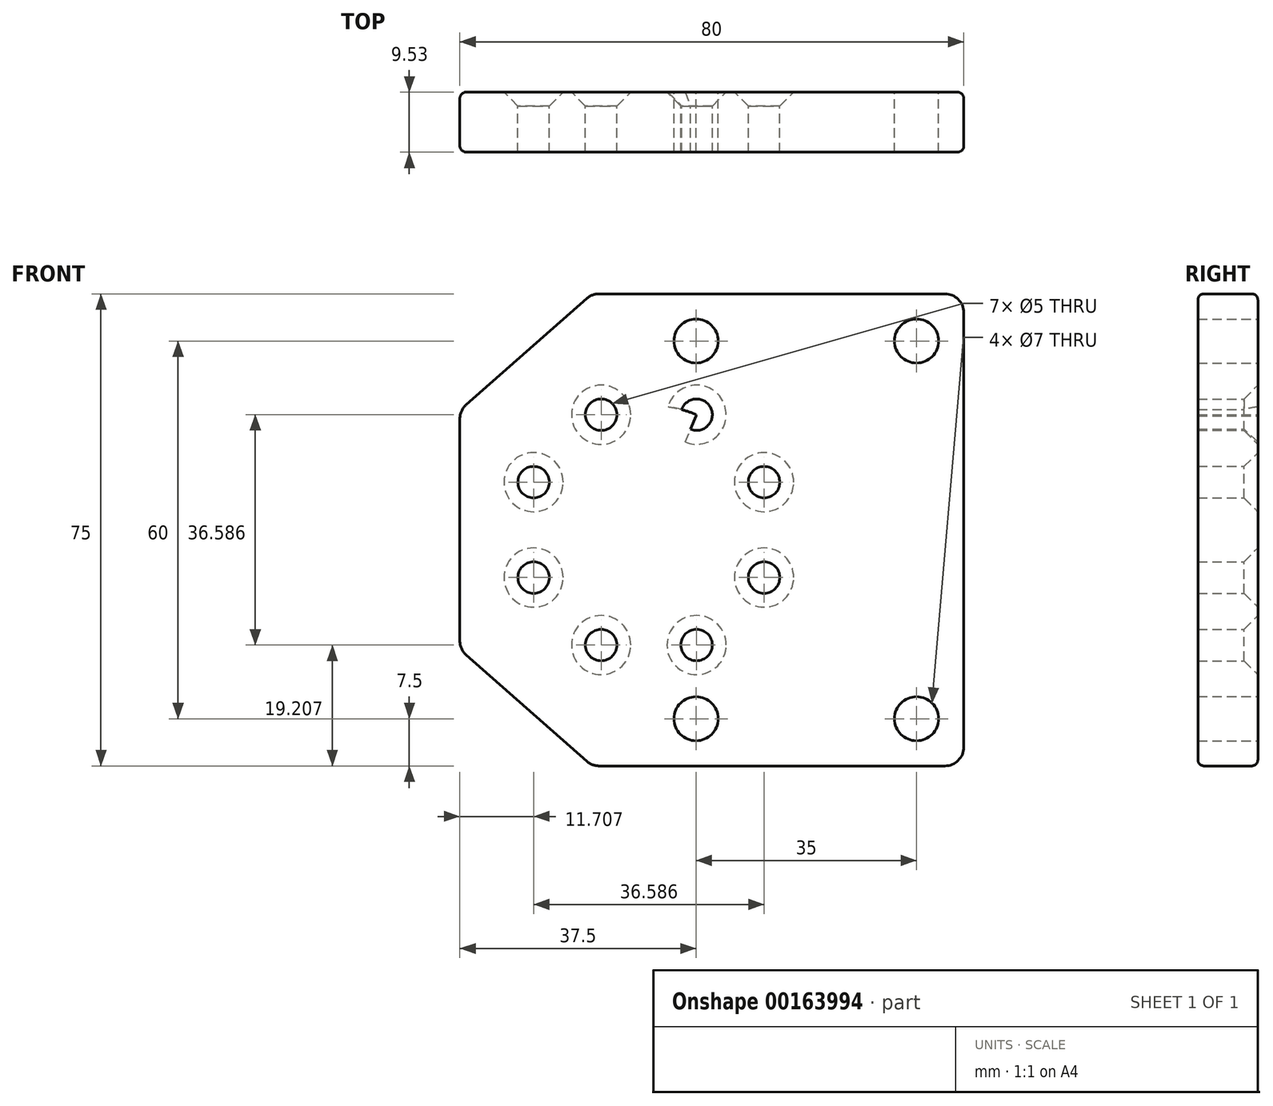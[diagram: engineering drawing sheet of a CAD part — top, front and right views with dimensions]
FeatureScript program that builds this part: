
annotation { "Feature Type Name" : "Feature", "Feature Type Description" : "" }
export const myFeature = defineFeature(function(context is Context, id is Id, definition is map)
    precondition{}
    {
        {
            var Q0;
            Q0=qCreatedBy(makeId("Front.planeOp"),FACE);
            var sketch = newSketch(context, id + "F0", { "sketchPlane" : qUnion([Q0])});
            skPoint(sketch, "E0.middle", {"position": v(0, 0) * mm});
            skCircle(sketch, "E1", {"center": v(0, 0) * mm, "radius": 19.8 * mm});
            skCircle(sketch, "E2", {"center": v(-7.58, 18.3) * mm, "radius": 2.5 * mm});
            skCircle(sketch, "E3", {"center": v(7.58, 18.3) * mm, "radius": 2.5 * mm});
            skCircle(sketch, "E4", {"center": v(18.3, 7.58) * mm, "radius": 2.5 * mm});
            skCircle(sketch, "E5", {"center": v(18.3, -7.58) * mm, "radius": 2.5 * mm});
            skCircle(sketch, "E6", {"center": v(7.58, -18.3) * mm, "radius": 2.5 * mm});
            skCircle(sketch, "E7", {"center": v(-7.58, -18.3) * mm, "radius": 2.5 * mm});
            skCircle(sketch, "E8", {"center": v(-18.3, -7.58) * mm, "radius": 2.5 * mm});
            skCircle(sketch, "E9", {"center": v(-18.3, 7.58) * mm, "radius": 2.5 * mm});
            skLineSegment(sketch, "E10", {"start": v(0, 0) * mm, "end": v(33.82, 81.64) * mm});
            skLineSegment(sketch, "E11", {"start": v(0, 0) * mm, "end": v(87.05, 36.06) * mm});
            skLineSegment(sketch, "E12", {"start": v(0, 0) * mm, "end": v(111.29, -46.1) * mm});
            skLineSegment(sketch, "E13", {"start": v(0, 0) * mm, "end": v(48.24, -116.46) * mm});
            skLineSegment(sketch, "E14", {"start": v(0, 0) * mm, "end": v(-47.93, -115.72) * mm});
            skLineSegment(sketch, "E15", {"start": v(0, 0) * mm, "end": v(-133.3, -55.22) * mm});
            skLineSegment(sketch, "E16", {"start": v(0, 0) * mm, "end": v(-127.93, 52.99) * mm});
            skLineSegment(sketch, "E17", {"start": v(0, 0) * mm, "end": v(-45.1, 108.86) * mm});
            skLineSegment(sketch, "E18.bottom", {"start": v(7.5, 30) * mm, "end": v(42.5, 30) * mm});
            skLineSegment(sketch, "E18.top", {"start": v(7.5, -30) * mm, "end": v(42.5, -30) * mm});
            skLineSegment(sketch, "E18.left", {"start": v(7.5, 30) * mm, "end": v(7.5, -30) * mm});
            skLineSegment(sketch, "E18.right", {"start": v(42.5, 30) * mm, "end": v(42.5, -30) * mm});
            skPoint(sketch, "E18.middle", {"position": v(25, 0) * mm});
            skCircle(sketch, "E19", {"center": v(7.5, 30) * mm, "radius": 3.5 * mm});
            skCircle(sketch, "E20", {"center": v(42.5, 30) * mm, "radius": 3.5 * mm});
            skCircle(sketch, "E21", {"center": v(42.5, -30) * mm, "radius": 3.5 * mm});
            skCircle(sketch, "E22", {"center": v(7.5, -30) * mm, "radius": 3.5 * mm});
            skLineSegment(sketch, "E23.bottom", {"start": v(50, 37.5) * mm, "end": v(-30, 37.5) * mm});
            skLineSegment(sketch, "E23.top", {"start": v(50, -37.5) * mm, "end": v(-30, -37.5) * mm});
            skLineSegment(sketch, "E23.left", {"start": v(50, 37.5) * mm, "end": v(50, -37.5) * mm});
            skLineSegment(sketch, "E23.right", {"start": v(-30, 37.5) * mm, "end": v(-30, -37.5) * mm});
            skPoint(sketch, "E23.middle", {"position": v(10, 0) * mm});
            skLineSegment(sketch, "E24", {"start": v(-30, 19) * mm, "end": v(-9, 37.5) * mm});
            skLineSegment(sketch, "E25", {"start": v(-30, -19) * mm, "end": v(-9, -37.5) * mm});
            skSolve(sketch);
        }
        {
            var Q0;
            {var subQ10=sQuery(id+"F0.wireOp",EDGE,"E0.right");var subQ13=sQuery(id+"F0.wireOp",EDGE,"E0.bottom");var subQ14=makeQuery(id+"F0.imprint","INTERSECT",VERTEX,{"derivedFrom":[subQ13,subQ10]});Q0=makeQuery(id+"F0.imprint","IMPRINT",FACE,{"disambiguationData":[TD([[makeQuery(id+"F0.imprint","IMPRINT",EDGE,{"disambiguationData":[TD([[subQ14,1.0]])],"derivedFrom":subQ13}),1.0]])]});}
            var Q1;
            {var subQ3=sQuery(id+"F0.wireOp",EDGE,"E16");var subQ9=sQuery(id+"F0.wireOp",EDGE,"E0.right");var subQ10=makeQuery(id+"F0.imprint","INTERSECT",VERTEX,{"derivedFrom":[subQ9,subQ3]});Q1=makeQuery(id+"F0.imprint","IMPRINT",FACE,{"disambiguationData":[TD([[makeQuery(id+"F0.imprint","IMPRINT",EDGE,{"disambiguationData":[TD([[subQ10,-1.0]])],"derivedFrom":subQ9}),1.0]])]});}
            var Q2;
            {var subQ9=sQuery(id+"F0.wireOp",EDGE,"E0.right");var subQ10=sQuery(id+"F0.wireOp",EDGE,"E0.top");var subQ11=makeQuery(id+"F0.imprint","INTERSECT",VERTEX,{"derivedFrom":[subQ10,subQ9]});Q2=makeQuery(id+"F0.imprint","IMPRINT",FACE,{"disambiguationData":[TD([[makeQuery(id+"F0.imprint","IMPRINT",EDGE,{"disambiguationData":[TD([[subQ11,1.0]])],"derivedFrom":subQ10}),-1.0]])]});}
            var Q3;
            {var subQ0=sQuery(id+"F0.wireOp",EDGE,"E13");var subQ1=sQuery(id+"F0.wireOp",EDGE,"E0.top");var subQ2=makeQuery(id+"F0.imprint","INTERSECT",VERTEX,{"derivedFrom":[subQ1,subQ0]});Q3=makeQuery(id+"F0.imprint","IMPRINT",FACE,{"disambiguationData":[TD([[makeQuery(id+"F0.imprint","IMPRINT",EDGE,{"disambiguationData":[TD([[subQ2,-1.0]])],"derivedFrom":subQ1}),-1.0]])]});}
            var Q4;
            {var subQ9=sQuery(id+"F0.wireOp",EDGE,"E0.left");var subQ10=sQuery(id+"F0.wireOp",EDGE,"E0.top");var subQ11=makeQuery(id+"F0.imprint","INTERSECT",VERTEX,{"derivedFrom":[subQ10,subQ9]});Q4=makeQuery(id+"F0.imprint","IMPRINT",FACE,{"disambiguationData":[TD([[makeQuery(id+"F0.imprint","IMPRINT",EDGE,{"disambiguationData":[TD([[subQ11,-1.0]])],"derivedFrom":subQ10}),-1.0]])]});}
            var Q5;
            {var subQ3=sQuery(id+"F0.wireOp",EDGE,"E11");var subQ9=sQuery(id+"F0.wireOp",EDGE,"E0.left");var subQ10=makeQuery(id+"F0.imprint","INTERSECT",VERTEX,{"derivedFrom":[subQ9,subQ3]});Q5=makeQuery(id+"F0.imprint","IMPRINT",FACE,{"disambiguationData":[TD([[makeQuery(id+"F0.imprint","IMPRINT",EDGE,{"disambiguationData":[TD([[subQ10,-1.0]])],"derivedFrom":subQ9}),-1.0]])]});}
            var Q6;
            {var subQ9=sQuery(id+"F0.wireOp",EDGE,"E0.left");var subQ10=sQuery(id+"F0.wireOp",EDGE,"E0.bottom");var subQ11=makeQuery(id+"F0.imprint","INTERSECT",VERTEX,{"derivedFrom":[subQ10,subQ9]});Q6=makeQuery(id+"F0.imprint","IMPRINT",FACE,{"disambiguationData":[TD([[makeQuery(id+"F0.imprint","IMPRINT",EDGE,{"disambiguationData":[TD([[subQ11,-1.0]])],"derivedFrom":subQ10}),1.0]])]});}
            var Q7;
            {var subQ0=sQuery(id+"F0.wireOp",EDGE,"E10");var subQ1=sQuery(id+"F0.wireOp",EDGE,"E0.bottom");var subQ2=makeQuery(id+"F0.imprint","INTERSECT",VERTEX,{"derivedFrom":[subQ1,subQ0]});Q7=makeQuery(id+"F0.imprint","IMPRINT",FACE,{"disambiguationData":[TD([[makeQuery(id+"F0.imprint","IMPRINT",EDGE,{"disambiguationData":[TD([[subQ2,-1.0]])],"derivedFrom":subQ1}),1.0]])]});}
            var Q8;
            {var subQ1=sQuery(id+"F0.wireOp",EDGE,"E1");var subQ9=sQuery(id+"F0.wireOp",EDGE,"E3");var subQ10=makeQuery(id+"F0.imprint","INTERSECT",VERTEX,{"disambiguationData":[OD(1.0)],"derivedFrom":[subQ1,subQ9]});Q8=makeQuery(id+"F0.imprint","IMPRINT",FACE,{"disambiguationData":[TD([[makeQuery(id+"F0.imprint","IMPRINT",EDGE,{"disambiguationData":[TD([[subQ10,-1.0]])],"derivedFrom":subQ1}),-1.0]])]});}
            var Q9;
            {var subQ9=sQuery(id+"F0.wireOp",EDGE,"E2");var subQ10=sQuery(id+"F0.wireOp",EDGE,"E1");var subQ11=makeQuery(id+"F0.imprint","INTERSECT",VERTEX,{"disambiguationData":[OD(1.0)],"derivedFrom":[subQ10,subQ9]});Q9=makeQuery(id+"F0.imprint","IMPRINT",FACE,{"disambiguationData":[TD([[makeQuery(id+"F0.imprint","IMPRINT",EDGE,{"disambiguationData":[TD([[subQ11,-1.0]])],"derivedFrom":subQ10}),-1.0]])]});}
            var Q10;
            {var subQ5=sQuery(id+"F0.wireOp",EDGE,"E1");var subQ7=sQuery(id+"F0.wireOp",EDGE,"E2");var subQ8=makeQuery(id+"F0.imprint","INTERSECT",VERTEX,{"disambiguationData":[OD(1.0)],"derivedFrom":[subQ5,subQ7]});Q10=makeQuery(id+"F0.imprint","IMPRINT",FACE,{"disambiguationData":[TD([[makeQuery(id+"F0.imprint","IMPRINT",EDGE,{"disambiguationData":[TD([[subQ8,-1.0]])],"derivedFrom":subQ5}),1.0]])]});}
            var Q11;
            {var subQ3=sQuery(id+"F0.wireOp",EDGE,"E3");var subQ6=sQuery(id+"F0.wireOp",EDGE,"E1");var subQ9=makeQuery(id+"F0.imprint","INTERSECT",VERTEX,{"disambiguationData":[OD(1.0)],"derivedFrom":[subQ6,subQ3]});Q11=makeQuery(id+"F0.imprint","IMPRINT",FACE,{"disambiguationData":[TD([[makeQuery(id+"F0.imprint","IMPRINT",EDGE,{"disambiguationData":[TD([[subQ9,-1.0]])],"derivedFrom":subQ6}),1.0]])]});}
            var Q12;
            {var subQ1=sQuery(id+"F0.wireOp",EDGE,"E1");var subQ7=sQuery(id+"F0.wireOp",EDGE,"E4");var subQ8=makeQuery(id+"F0.imprint","INTERSECT",VERTEX,{"disambiguationData":[OD(1.0)],"derivedFrom":[subQ1,subQ7]});Q12=makeQuery(id+"F0.imprint","IMPRINT",FACE,{"disambiguationData":[TD([[makeQuery(id+"F0.imprint","IMPRINT",EDGE,{"disambiguationData":[TD([[subQ8,-1.0]])],"derivedFrom":subQ1}),1.0]])]});}
            var Q13;
            {var subQ3=sQuery(id+"F0.wireOp",EDGE,"E4");var subQ6=sQuery(id+"F0.wireOp",EDGE,"jBsVCdZr-T46d-phkG-uXee-YsdgyrdP6RDM.left");var subQ9=makeQuery(id+"F0.imprint","INTERSECT",VERTEX,{"disambiguationData":[OD(1.0)],"derivedFrom":[subQ6,subQ3]});Q13=makeQuery(id+"F0.imprint","IMPRINT",FACE,{"disambiguationData":[TD([[makeQuery(id+"F0.imprint","IMPRINT",EDGE,{"disambiguationData":[TD([[subQ9,-1.0]])],"derivedFrom":subQ6}),-1.0]])]});}
            var Q14;
            {var subQ0=sQuery(id+"F0.wireOp",EDGE,"E4");var subQ1=sQuery(id+"F0.wireOp",EDGE,"E1");var subQ2=makeQuery(id+"F0.imprint","INTERSECT",VERTEX,{"disambiguationData":[OD(0.0)],"derivedFrom":[subQ1,subQ0]});Q14=makeQuery(id+"F0.imprint","IMPRINT",FACE,{"disambiguationData":[TD([[makeQuery(id+"F0.imprint","IMPRINT",EDGE,{"disambiguationData":[TD([[subQ2,1.0]])],"derivedFrom":subQ1}),1.0]])]});}
            var Q15;
            {var subQ5=sQuery(id+"F0.wireOp",EDGE,"E6");var subQ6=sQuery(id+"F0.wireOp",EDGE,"E1");var subQ7=makeQuery(id+"F0.imprint","INTERSECT",VERTEX,{"disambiguationData":[OD(1.0)],"derivedFrom":[subQ6,subQ5]});Q15=makeQuery(id+"F0.imprint","IMPRINT",FACE,{"disambiguationData":[TD([[makeQuery(id+"F0.imprint","IMPRINT",EDGE,{"disambiguationData":[TD([[subQ7,-1.0]])],"derivedFrom":subQ6}),1.0]])]});}
            var Q16;
            {var subQ9=sQuery(id+"F0.wireOp",EDGE,"E6");var subQ10=sQuery(id+"F0.wireOp",EDGE,"E1");var subQ11=makeQuery(id+"F0.imprint","INTERSECT",VERTEX,{"disambiguationData":[OD(1.0)],"derivedFrom":[subQ10,subQ9]});Q16=makeQuery(id+"F0.imprint","IMPRINT",FACE,{"disambiguationData":[TD([[makeQuery(id+"F0.imprint","IMPRINT",EDGE,{"disambiguationData":[TD([[subQ11,-1.0]])],"derivedFrom":subQ10}),-1.0]])]});}
            var Q17;
            {var subQ1=sQuery(id+"F0.wireOp",EDGE,"E1");var subQ5=sQuery(id+"F0.wireOp",EDGE,"E7");var subQ6=makeQuery(id+"F0.imprint","INTERSECT",VERTEX,{"disambiguationData":[OD(1.0)],"derivedFrom":[subQ1,subQ5]});Q17=makeQuery(id+"F0.imprint","IMPRINT",FACE,{"disambiguationData":[TD([[makeQuery(id+"F0.imprint","IMPRINT",EDGE,{"disambiguationData":[TD([[subQ6,-1.0]])],"derivedFrom":subQ1}),-1.0]])]});}
            var Q18;
            {var subQ5=sQuery(id+"F0.wireOp",EDGE,"E7");var subQ6=sQuery(id+"F0.wireOp",EDGE,"E1");var subQ7=makeQuery(id+"F0.imprint","INTERSECT",VERTEX,{"disambiguationData":[OD(1.0)],"derivedFrom":[subQ6,subQ5]});Q18=makeQuery(id+"F0.imprint","IMPRINT",FACE,{"disambiguationData":[TD([[makeQuery(id+"F0.imprint","IMPRINT",EDGE,{"disambiguationData":[TD([[subQ7,-1.0]])],"derivedFrom":subQ6}),1.0]])]});}
            var Q19;
            {var subQ5=sQuery(id+"F0.wireOp",EDGE,"E8");var subQ6=sQuery(id+"F0.wireOp",EDGE,"E1");var subQ7=makeQuery(id+"F0.imprint","INTERSECT",VERTEX,{"disambiguationData":[OD(1.0)],"derivedFrom":[subQ6,subQ5]});Q19=makeQuery(id+"F0.imprint","IMPRINT",FACE,{"disambiguationData":[TD([[makeQuery(id+"F0.imprint","IMPRINT",EDGE,{"disambiguationData":[TD([[subQ7,-1.0]])],"derivedFrom":subQ6}),1.0]])]});}
            var Q20;
            {var subQ5=sQuery(id+"F0.wireOp",EDGE,"jBsVCdZr-T46d-phkG-uXee-YsdgyrdP6RDM.right");var subQ7=sQuery(id+"F0.wireOp",EDGE,"E9");var subQ8=makeQuery(id+"F0.imprint","INTERSECT",VERTEX,{"disambiguationData":[OD(1.0)],"derivedFrom":[subQ5,subQ7]});Q20=makeQuery(id+"F0.imprint","IMPRINT",FACE,{"disambiguationData":[TD([[makeQuery(id+"F0.imprint","IMPRINT",EDGE,{"disambiguationData":[TD([[subQ8,-1.0]])],"derivedFrom":subQ5}),1.0]])]});}
            var Q21;
            {var subQ0=sQuery(id+"F0.wireOp",EDGE,"E9");var subQ1=sQuery(id+"F0.wireOp",EDGE,"E1");var subQ2=makeQuery(id+"F0.imprint","INTERSECT",VERTEX,{"disambiguationData":[OD(1.0)],"derivedFrom":[subQ1,subQ0]});Q21=makeQuery(id+"F0.imprint","IMPRINT",FACE,{"disambiguationData":[TD([[makeQuery(id+"F0.imprint","IMPRINT",EDGE,{"disambiguationData":[TD([[subQ2,-1.0]])],"derivedFrom":subQ1}),1.0]])]});}
            var Q22;
            {var subQ5=sQuery(id+"F0.wireOp",EDGE,"E8");var subQ6=sQuery(id+"F0.wireOp",EDGE,"E1");var subQ7=makeQuery(id+"F0.imprint","INTERSECT",VERTEX,{"disambiguationData":[OD(1.0)],"derivedFrom":[subQ6,subQ5]});Q22=makeQuery(id+"F0.imprint","IMPRINT",FACE,{"disambiguationData":[TD([[makeQuery(id+"F0.imprint","IMPRINT",EDGE,{"disambiguationData":[TD([[subQ7,-1.0]])],"derivedFrom":subQ6}),-1.0]])]});}
            var Q23;
            {var subQ7=sQuery(id+"F0.wireOp",EDGE,"E4");var subQ8=sQuery(id+"F0.wireOp",EDGE,"E1");var subQ9=makeQuery(id+"F0.imprint","INTERSECT",VERTEX,{"disambiguationData":[OD(1.0)],"derivedFrom":[subQ8,subQ7]});Q23=makeQuery(id+"F0.imprint","IMPRINT",FACE,{"disambiguationData":[TD([[makeQuery(id+"F0.imprint","IMPRINT",EDGE,{"disambiguationData":[TD([[subQ9,-1.0]])],"derivedFrom":subQ8}),-1.0]])]});}
            var Q24;
            {var subQ6=sQuery(id+"F0.wireOp",EDGE,"E10");var subQ11=sQuery(id+"F0.wireOp",EDGE,"E23.bottom");var subQ12=makeQuery(id+"F0.imprint","INTERSECT",VERTEX,{"derivedFrom":[subQ6,subQ11]});Q24=makeQuery(id+"F0.imprint","IMPRINT",FACE,{"disambiguationData":[TD([[makeQuery(id+"F0.imprint","IMPRINT",EDGE,{"disambiguationData":[TD([[subQ12,1.0]])],"derivedFrom":subQ6}),-1.0]])]});}
            var Q25;
            {var subQ0=sQuery(id+"F0.wireOp",EDGE,"E9");var subQ1=sQuery(id+"F0.wireOp",EDGE,"E1");var subQ2=makeQuery(id+"F0.imprint","INTERSECT",VERTEX,{"disambiguationData":[OD(1.0)],"derivedFrom":[subQ1,subQ0]});Q25=makeQuery(id+"F0.imprint","IMPRINT",FACE,{"disambiguationData":[TD([[makeQuery(id+"F0.imprint","IMPRINT",EDGE,{"disambiguationData":[TD([[subQ2,-1.0]])],"derivedFrom":subQ1}),-1.0]])]});}
            var Q26;
            {var subQ1=sQuery(id+"F0.wireOp",EDGE,"E4");var subQ9=sQuery(id+"F0.wireOp",EDGE,"E1");var subQ10=makeQuery(id+"F0.imprint","INTERSECT",VERTEX,{"disambiguationData":[OD(0.0)],"derivedFrom":[subQ9,subQ1]});Q26=makeQuery(id+"F0.imprint","IMPRINT",FACE,{"disambiguationData":[TD([[makeQuery(id+"F0.imprint","IMPRINT",EDGE,{"disambiguationData":[TD([[subQ10,1.0]])],"derivedFrom":subQ9}),-1.0]])]});}
            var Q27;
            {var subQ0=sQuery(id+"F0.wireOp",EDGE,"E23.left");var subQ1=sQuery(id+"F0.wireOp",EDGE,"E11");var subQ2=makeQuery(id+"F0.imprint","INTERSECT",VERTEX,{"derivedFrom":[subQ1,subQ0]});Q27=makeQuery(id+"F0.imprint","IMPRINT",FACE,{"disambiguationData":[TD([[makeQuery(id+"F0.imprint","IMPRINT",EDGE,{"disambiguationData":[TD([[subQ2,1.0]])],"derivedFrom":subQ1}),-1.0]])]});}
            var Q28;
            {var subQ1=sQuery(id+"F0.wireOp",EDGE,"E12");var subQ11=sQuery(id+"F0.wireOp",EDGE,"E23.left");var subQ12=makeQuery(id+"F0.imprint","INTERSECT",VERTEX,{"derivedFrom":[subQ1,subQ11]});Q28=makeQuery(id+"F0.imprint","IMPRINT",FACE,{"disambiguationData":[TD([[makeQuery(id+"F0.imprint","IMPRINT",EDGE,{"disambiguationData":[TD([[subQ12,1.0]])],"derivedFrom":subQ1}),-1.0]])]});}
            var Q29;
            {var subQ1=sQuery(id+"F0.wireOp",EDGE,"E12");var subQ3=sQuery(id+"F0.wireOp",EDGE,"E18.left");var subQ4=makeQuery(id+"F0.imprint","INTERSECT",VERTEX,{"derivedFrom":[subQ1,subQ3]});Q29=makeQuery(id+"F0.imprint","IMPRINT",FACE,{"disambiguationData":[TD([[makeQuery(id+"F0.imprint","IMPRINT",EDGE,{"disambiguationData":[TD([[subQ4,-1.0]])],"derivedFrom":subQ3}),-1.0]])]});}
            var Q30;
            {var subQ1=sQuery(id+"F0.wireOp",EDGE,"E11");var subQ3=sQuery(id+"F0.wireOp",EDGE,"E18.left");var subQ4=makeQuery(id+"F0.imprint","INTERSECT",VERTEX,{"derivedFrom":[subQ1,subQ3]});Q30=makeQuery(id+"F0.imprint","IMPRINT",FACE,{"disambiguationData":[TD([[makeQuery(id+"F0.imprint","IMPRINT",EDGE,{"disambiguationData":[TD([[subQ4,-1.0]])],"derivedFrom":subQ3}),-1.0]])]});}
            var Q31;
            {var subQ0=sQuery(id+"F0.wireOp",EDGE,"E18.left");var subQ1=sQuery(id+"F0.wireOp",EDGE,"E1");var subQ2=makeQuery(id+"F0.imprint","INTERSECT",VERTEX,{"disambiguationData":[OD(1.0)],"derivedFrom":[subQ1,subQ0]});Q31=makeQuery(id+"F0.imprint","IMPRINT",FACE,{"disambiguationData":[TD([[makeQuery(id+"F0.imprint","IMPRINT",EDGE,{"disambiguationData":[TD([[subQ2,-1.0]])],"derivedFrom":subQ1}),1.0]])]});}
            var Q32;
            {var subQ0=sQuery(id+"F0.wireOp",EDGE,"E10");var subQ1=sQuery(id+"F0.wireOp",EDGE,"E3");var subQ2=makeQuery(id+"F0.imprint","INTERSECT",VERTEX,{"disambiguationData":[OD(1.0)],"derivedFrom":[subQ1,subQ0]});Q32=makeQuery(id+"F0.imprint","IMPRINT",FACE,{"disambiguationData":[TD([[makeQuery(id+"F0.imprint","IMPRINT",EDGE,{"disambiguationData":[TD([[subQ2,-1.0]])],"derivedFrom":subQ1}),-1.0]])]});}
            var Q33;
            {var subQ0=sQuery(id+"F0.wireOp",EDGE,"E18.left");var subQ1=sQuery(id+"F0.wireOp",EDGE,"E6");var subQ2=makeQuery(id+"F0.imprint","INTERSECT",VERTEX,{"disambiguationData":[OD(1.0)],"derivedFrom":[subQ1,subQ0]});Q33=makeQuery(id+"F0.imprint","IMPRINT",FACE,{"disambiguationData":[TD([[makeQuery(id+"F0.imprint","IMPRINT",EDGE,{"disambiguationData":[TD([[subQ2,-1.0]])],"derivedFrom":subQ1}),-1.0]])]});}
            var Q34;
            {var subQ0=sQuery(id+"F0.wireOp",EDGE,"E18.left");var subQ1=sQuery(id+"F0.wireOp",EDGE,"E3");var subQ2=makeQuery(id+"F0.imprint","INTERSECT",VERTEX,{"disambiguationData":[OD(0.0)],"derivedFrom":[subQ1,subQ0]});Q34=makeQuery(id+"F0.imprint","IMPRINT",FACE,{"disambiguationData":[TD([[makeQuery(id+"F0.imprint","IMPRINT",EDGE,{"disambiguationData":[TD([[subQ2,1.0]])],"derivedFrom":subQ1}),-1.0]])]});}
            extrude(context, id + "F1", {"entities" : qUnion([Q0, Q1, Q2, Q3, Q4, Q5, Q6, Q7, Q8, Q9, Q10, Q11, Q12, Q13, Q14, Q15, Q16, Q17, Q18, Q19, Q20, Q21, Q22, Q23, Q24, Q25, Q26, Q27, Q28, Q29, Q30, Q31, Q32, Q33, Q34]), "depth" : 9.52 * mm});
        }
        {
            var Q0;
            Q0=makeQuery(id+"F1.opExtrude","CAP_EDGE",EDGE,{"disambiguationData":[OSD([sQuery(id+"F0.wireOp",EDGE,"E3")])],"isStart":true});
            var Q1;
            Q1=makeQuery(id+"F1.opExtrude","CAP_EDGE",EDGE,{"disambiguationData":[OSD([sQuery(id+"F0.wireOp",EDGE,"E2")])],"isStart":true});
            var Q2;
            Q2=makeQuery(id+"F1.opExtrude","CAP_EDGE",EDGE,{"disambiguationData":[OSD([sQuery(id+"F0.wireOp",EDGE,"E9")])],"isStart":true});
            var Q3;
            Q3=makeQuery(id+"F1.opExtrude","CAP_EDGE",EDGE,{"disambiguationData":[OSD([sQuery(id+"F0.wireOp",EDGE,"E8")])],"isStart":true});
            var Q4;
            Q4=makeQuery(id+"F1.opExtrude","CAP_EDGE",EDGE,{"disambiguationData":[OSD([sQuery(id+"F0.wireOp",EDGE,"E7")])],"isStart":true});
            var Q5;
            Q5=makeQuery(id+"F1.opExtrude","CAP_EDGE",EDGE,{"disambiguationData":[OSD([sQuery(id+"F0.wireOp",EDGE,"E6")])],"isStart":true});
            var Q6;
            Q6=makeQuery(id+"F1.opExtrude","CAP_EDGE",EDGE,{"disambiguationData":[OSD([sQuery(id+"F0.wireOp",EDGE,"E5")])],"isStart":true});
            var Q7;
            Q7=makeQuery(id+"F1.opExtrude","CAP_EDGE",EDGE,{"disambiguationData":[OSD([sQuery(id+"F0.wireOp",EDGE,"E4")])],"isStart":true});
            chamfer(context, id + "F2", {"entities" : qUnion([Q0, Q1, Q2, Q3, Q4, Q5, Q6, Q7]), "width" : 2.2 * mm, "tangentPropagation" : true});
        }
        {
            var Q0;
            Q0=makeQuery(id+"F1.opExtrude","SWEPT_EDGE",EDGE,{"disambiguationData":[OSD([sQuery(id+"F0.wireOp",EDGE,"E23.bottom"),sQuery(id+"F0.wireOp",EDGE,"E23.left")])]});
            var Q1;
            Q1=makeQuery(id+"F1.opExtrude","SWEPT_EDGE",EDGE,{"disambiguationData":[OSD([sQuery(id+"F0.wireOp",EDGE,"E23.bottom"),sQuery(id+"F0.wireOp",EDGE,"E23.right")])]});
            var Q2;
            Q2=makeQuery(id+"F1.opExtrude","SWEPT_EDGE",EDGE,{"disambiguationData":[OSD([sQuery(id+"F0.wireOp",EDGE,"E23.top"),sQuery(id+"F0.wireOp",EDGE,"E23.left")])]});
            var Q3;
            Q3=makeQuery(id+"F1.opExtrude","SWEPT_EDGE",EDGE,{"disambiguationData":[OSD([sQuery(id+"F0.wireOp",EDGE,"E23.top"),sQuery(id+"F0.wireOp",EDGE,"E23.right")])]});
            fillet(context, id + "F3", {"entities" : qUnion([Q0, Q1, Q2, Q3]), "radius" : 3 * mm, "tangentPropagation" : true, "allowEdgeOverflow" : false});
        }
        {
            var Q0;
            Q0=makeQuery(id+"F1.opExtrude","CAP_EDGE",EDGE,{"disambiguationData":[OSD([sQuery(id+"F0.wireOp",EDGE,"E23.bottom")])],"isStart":false});
            var Q1;
            Q1=makeQuery(id+"F1.opExtrude","CAP_EDGE",EDGE,{"disambiguationData":[OSD([sQuery(id+"F0.wireOp",EDGE,"E23.right")])],"isStart":false});
            var Q2;
            Q2=makeQuery(id+"F1.opExtrude","CAP_EDGE",EDGE,{"disambiguationData":[OSD([sQuery(id+"F0.wireOp",EDGE,"E23.top")])],"isStart":false});
            var Q3;
            Q3=makeQuery(id+"F1.opExtrude","CAP_EDGE",EDGE,{"disambiguationData":[OSD([sQuery(id+"F0.wireOp",EDGE,"E23.left")])],"isStart":false});
            var Q4;
            Q4=makeQuery(id+"F1.opExtrude","CAP_EDGE",EDGE,{"disambiguationData":[OSD([sQuery(id+"F0.wireOp",EDGE,"E23.left")])],"isStart":true});
            var Q5;
            Q5=makeQuery(id+"F1.opExtrude","CAP_EDGE",EDGE,{"disambiguationData":[OSD([sQuery(id+"F0.wireOp",EDGE,"E23.bottom")])],"isStart":true});
            var Q6;
            Q6=makeQuery(id+"F1.opExtrude","CAP_EDGE",EDGE,{"disambiguationData":[OSD([sQuery(id+"F0.wireOp",EDGE,"E23.right")])],"isStart":true});
            var Q7;
            Q7=makeQuery(id+"F1.opExtrude","CAP_EDGE",EDGE,{"disambiguationData":[OSD([sQuery(id+"F0.wireOp",EDGE,"E23.top")])],"isStart":true});
            var Q8;
            {var subQ0=sQuery(id+"F0.wireOp",EDGE,"E23.left");var subQ1=sQuery(id+"F0.wireOp",EDGE,"E23.bottom");Q8=makeQuery(id+"F3.opFillet","BLEND_EDGE",EDGE,{"blendedFrom":[makeQuery(id+"F1.opExtrude","SWEPT_EDGE",EDGE,{"disambiguationData":[OSD([subQ1,subQ0])]}),makeQuery(id+"F1.opExtrude","CAP_FACE",FACE,{"disambiguationData":[OSD([sQuery(id+"F0.wireOp",EDGE,"E2"),sQuery(id+"F0.wireOp",EDGE,"E3"),sQuery(id+"F0.wireOp",EDGE,"E4"),sQuery(id+"F0.wireOp",EDGE,"E5"),sQuery(id+"F0.wireOp",EDGE,"E6"),sQuery(id+"F0.wireOp",EDGE,"E7"),sQuery(id+"F0.wireOp",EDGE,"E8"),sQuery(id+"F0.wireOp",EDGE,"E9"),sQuery(id+"F0.wireOp",EDGE,"E19"),sQuery(id+"F0.wireOp",EDGE,"E20"),sQuery(id+"F0.wireOp",EDGE,"E21"),sQuery(id+"F0.wireOp",EDGE,"E22"),subQ1,sQuery(id+"F0.wireOp",EDGE,"E23.top"),subQ0,sQuery(id+"F0.wireOp",EDGE,"E23.right")])],"isStart":false})],"blendedInto":[makeQuery(id+"F1.opExtrude","CAP_FACE",FACE,{"disambiguationData":[OSD([sQuery(id+"F0.wireOp",EDGE,"E2"),sQuery(id+"F0.wireOp",EDGE,"E3"),sQuery(id+"F0.wireOp",EDGE,"E4"),sQuery(id+"F0.wireOp",EDGE,"E5"),sQuery(id+"F0.wireOp",EDGE,"E6"),sQuery(id+"F0.wireOp",EDGE,"E7"),sQuery(id+"F0.wireOp",EDGE,"E8"),sQuery(id+"F0.wireOp",EDGE,"E9"),sQuery(id+"F0.wireOp",EDGE,"E19"),sQuery(id+"F0.wireOp",EDGE,"E20"),sQuery(id+"F0.wireOp",EDGE,"E21"),sQuery(id+"F0.wireOp",EDGE,"E22"),subQ1,sQuery(id+"F0.wireOp",EDGE,"E23.top"),subQ0,sQuery(id+"F0.wireOp",EDGE,"E23.right")])],"isStart":false})]});}
            var Q9;
            {var subQ0=sQuery(id+"F0.wireOp",EDGE,"E23.left");var subQ1=sQuery(id+"F0.wireOp",EDGE,"E23.bottom");Q9=makeQuery(id+"F3.opFillet","BLEND_EDGE",EDGE,{"blendedFrom":[makeQuery(id+"F1.opExtrude","SWEPT_EDGE",EDGE,{"disambiguationData":[OSD([subQ1,subQ0])]}),makeQuery(id+"F1.opExtrude","CAP_FACE",FACE,{"disambiguationData":[OSD([sQuery(id+"F0.wireOp",EDGE,"E2"),sQuery(id+"F0.wireOp",EDGE,"E3"),sQuery(id+"F0.wireOp",EDGE,"E4"),sQuery(id+"F0.wireOp",EDGE,"E5"),sQuery(id+"F0.wireOp",EDGE,"E6"),sQuery(id+"F0.wireOp",EDGE,"E7"),sQuery(id+"F0.wireOp",EDGE,"E8"),sQuery(id+"F0.wireOp",EDGE,"E9"),sQuery(id+"F0.wireOp",EDGE,"E19"),sQuery(id+"F0.wireOp",EDGE,"E20"),sQuery(id+"F0.wireOp",EDGE,"E21"),sQuery(id+"F0.wireOp",EDGE,"E22"),subQ1,sQuery(id+"F0.wireOp",EDGE,"E23.top"),subQ0,sQuery(id+"F0.wireOp",EDGE,"E23.right")])],"isStart":true})],"blendedInto":[makeQuery(id+"F1.opExtrude","CAP_FACE",FACE,{"disambiguationData":[OSD([sQuery(id+"F0.wireOp",EDGE,"E2"),sQuery(id+"F0.wireOp",EDGE,"E3"),sQuery(id+"F0.wireOp",EDGE,"E4"),sQuery(id+"F0.wireOp",EDGE,"E5"),sQuery(id+"F0.wireOp",EDGE,"E6"),sQuery(id+"F0.wireOp",EDGE,"E7"),sQuery(id+"F0.wireOp",EDGE,"E8"),sQuery(id+"F0.wireOp",EDGE,"E9"),sQuery(id+"F0.wireOp",EDGE,"E19"),sQuery(id+"F0.wireOp",EDGE,"E20"),sQuery(id+"F0.wireOp",EDGE,"E21"),sQuery(id+"F0.wireOp",EDGE,"E22"),subQ1,sQuery(id+"F0.wireOp",EDGE,"E23.top"),subQ0,sQuery(id+"F0.wireOp",EDGE,"E23.right")])],"isStart":true})]});}
            var Q10;
            {var subQ0=sQuery(id+"F0.wireOp",EDGE,"E23.left");var subQ1=sQuery(id+"F0.wireOp",EDGE,"E23.top");Q10=makeQuery(id+"F3.opFillet","BLEND_EDGE",EDGE,{"blendedFrom":[makeQuery(id+"F1.opExtrude","SWEPT_EDGE",EDGE,{"disambiguationData":[OSD([subQ1,subQ0])]}),makeQuery(id+"F1.opExtrude","CAP_FACE",FACE,{"disambiguationData":[OSD([sQuery(id+"F0.wireOp",EDGE,"E2"),sQuery(id+"F0.wireOp",EDGE,"E3"),sQuery(id+"F0.wireOp",EDGE,"E4"),sQuery(id+"F0.wireOp",EDGE,"E5"),sQuery(id+"F0.wireOp",EDGE,"E6"),sQuery(id+"F0.wireOp",EDGE,"E7"),sQuery(id+"F0.wireOp",EDGE,"E8"),sQuery(id+"F0.wireOp",EDGE,"E9"),sQuery(id+"F0.wireOp",EDGE,"E19"),sQuery(id+"F0.wireOp",EDGE,"E20"),sQuery(id+"F0.wireOp",EDGE,"E21"),sQuery(id+"F0.wireOp",EDGE,"E22"),sQuery(id+"F0.wireOp",EDGE,"E23.bottom"),subQ1,subQ0,sQuery(id+"F0.wireOp",EDGE,"E23.right")])],"isStart":false})],"blendedInto":[makeQuery(id+"F1.opExtrude","CAP_FACE",FACE,{"disambiguationData":[OSD([sQuery(id+"F0.wireOp",EDGE,"E2"),sQuery(id+"F0.wireOp",EDGE,"E3"),sQuery(id+"F0.wireOp",EDGE,"E4"),sQuery(id+"F0.wireOp",EDGE,"E5"),sQuery(id+"F0.wireOp",EDGE,"E6"),sQuery(id+"F0.wireOp",EDGE,"E7"),sQuery(id+"F0.wireOp",EDGE,"E8"),sQuery(id+"F0.wireOp",EDGE,"E9"),sQuery(id+"F0.wireOp",EDGE,"E19"),sQuery(id+"F0.wireOp",EDGE,"E20"),sQuery(id+"F0.wireOp",EDGE,"E21"),sQuery(id+"F0.wireOp",EDGE,"E22"),sQuery(id+"F0.wireOp",EDGE,"E23.bottom"),subQ1,subQ0,sQuery(id+"F0.wireOp",EDGE,"E23.right")])],"isStart":false})]});}
            var Q11;
            {var subQ0=sQuery(id+"F0.wireOp",EDGE,"E23.left");var subQ1=sQuery(id+"F0.wireOp",EDGE,"E23.top");Q11=makeQuery(id+"F3.opFillet","BLEND_EDGE",EDGE,{"blendedFrom":[makeQuery(id+"F1.opExtrude","SWEPT_EDGE",EDGE,{"disambiguationData":[OSD([subQ1,subQ0])]}),makeQuery(id+"F1.opExtrude","CAP_FACE",FACE,{"disambiguationData":[OSD([sQuery(id+"F0.wireOp",EDGE,"E2"),sQuery(id+"F0.wireOp",EDGE,"E3"),sQuery(id+"F0.wireOp",EDGE,"E4"),sQuery(id+"F0.wireOp",EDGE,"E5"),sQuery(id+"F0.wireOp",EDGE,"E6"),sQuery(id+"F0.wireOp",EDGE,"E7"),sQuery(id+"F0.wireOp",EDGE,"E8"),sQuery(id+"F0.wireOp",EDGE,"E9"),sQuery(id+"F0.wireOp",EDGE,"E19"),sQuery(id+"F0.wireOp",EDGE,"E20"),sQuery(id+"F0.wireOp",EDGE,"E21"),sQuery(id+"F0.wireOp",EDGE,"E22"),sQuery(id+"F0.wireOp",EDGE,"E23.bottom"),subQ1,subQ0,sQuery(id+"F0.wireOp",EDGE,"E23.right")])],"isStart":true})],"blendedInto":[makeQuery(id+"F1.opExtrude","CAP_FACE",FACE,{"disambiguationData":[OSD([sQuery(id+"F0.wireOp",EDGE,"E2"),sQuery(id+"F0.wireOp",EDGE,"E3"),sQuery(id+"F0.wireOp",EDGE,"E4"),sQuery(id+"F0.wireOp",EDGE,"E5"),sQuery(id+"F0.wireOp",EDGE,"E6"),sQuery(id+"F0.wireOp",EDGE,"E7"),sQuery(id+"F0.wireOp",EDGE,"E8"),sQuery(id+"F0.wireOp",EDGE,"E9"),sQuery(id+"F0.wireOp",EDGE,"E19"),sQuery(id+"F0.wireOp",EDGE,"E20"),sQuery(id+"F0.wireOp",EDGE,"E21"),sQuery(id+"F0.wireOp",EDGE,"E22"),sQuery(id+"F0.wireOp",EDGE,"E23.bottom"),subQ1,subQ0,sQuery(id+"F0.wireOp",EDGE,"E23.right")])],"isStart":true})]});}
            var Q12;
            {var subQ0=sQuery(id+"F0.wireOp",EDGE,"E23.right");var subQ1=sQuery(id+"F0.wireOp",EDGE,"E23.top");Q12=makeQuery(id+"F3.opFillet","BLEND_EDGE",EDGE,{"blendedFrom":[makeQuery(id+"F1.opExtrude","SWEPT_EDGE",EDGE,{"disambiguationData":[OSD([subQ1,subQ0])]}),makeQuery(id+"F1.opExtrude","CAP_FACE",FACE,{"disambiguationData":[OSD([sQuery(id+"F0.wireOp",EDGE,"E2"),sQuery(id+"F0.wireOp",EDGE,"E3"),sQuery(id+"F0.wireOp",EDGE,"E4"),sQuery(id+"F0.wireOp",EDGE,"E5"),sQuery(id+"F0.wireOp",EDGE,"E6"),sQuery(id+"F0.wireOp",EDGE,"E7"),sQuery(id+"F0.wireOp",EDGE,"E8"),sQuery(id+"F0.wireOp",EDGE,"E9"),sQuery(id+"F0.wireOp",EDGE,"E19"),sQuery(id+"F0.wireOp",EDGE,"E20"),sQuery(id+"F0.wireOp",EDGE,"E21"),sQuery(id+"F0.wireOp",EDGE,"E22"),sQuery(id+"F0.wireOp",EDGE,"E23.bottom"),subQ1,sQuery(id+"F0.wireOp",EDGE,"E23.left"),subQ0])],"isStart":false})],"blendedInto":[makeQuery(id+"F1.opExtrude","CAP_FACE",FACE,{"disambiguationData":[OSD([sQuery(id+"F0.wireOp",EDGE,"E2"),sQuery(id+"F0.wireOp",EDGE,"E3"),sQuery(id+"F0.wireOp",EDGE,"E4"),sQuery(id+"F0.wireOp",EDGE,"E5"),sQuery(id+"F0.wireOp",EDGE,"E6"),sQuery(id+"F0.wireOp",EDGE,"E7"),sQuery(id+"F0.wireOp",EDGE,"E8"),sQuery(id+"F0.wireOp",EDGE,"E9"),sQuery(id+"F0.wireOp",EDGE,"E19"),sQuery(id+"F0.wireOp",EDGE,"E20"),sQuery(id+"F0.wireOp",EDGE,"E21"),sQuery(id+"F0.wireOp",EDGE,"E22"),sQuery(id+"F0.wireOp",EDGE,"E23.bottom"),subQ1,sQuery(id+"F0.wireOp",EDGE,"E23.left"),subQ0])],"isStart":false})]});}
            var Q13;
            {var subQ0=sQuery(id+"F0.wireOp",EDGE,"E23.right");var subQ1=sQuery(id+"F0.wireOp",EDGE,"E23.bottom");Q13=makeQuery(id+"F3.opFillet","BLEND_EDGE",EDGE,{"blendedFrom":[makeQuery(id+"F1.opExtrude","SWEPT_EDGE",EDGE,{"disambiguationData":[OSD([subQ1,subQ0])]}),makeQuery(id+"F1.opExtrude","CAP_FACE",FACE,{"disambiguationData":[OSD([sQuery(id+"F0.wireOp",EDGE,"E2"),sQuery(id+"F0.wireOp",EDGE,"E3"),sQuery(id+"F0.wireOp",EDGE,"E4"),sQuery(id+"F0.wireOp",EDGE,"E5"),sQuery(id+"F0.wireOp",EDGE,"E6"),sQuery(id+"F0.wireOp",EDGE,"E7"),sQuery(id+"F0.wireOp",EDGE,"E8"),sQuery(id+"F0.wireOp",EDGE,"E9"),sQuery(id+"F0.wireOp",EDGE,"E19"),sQuery(id+"F0.wireOp",EDGE,"E20"),sQuery(id+"F0.wireOp",EDGE,"E21"),sQuery(id+"F0.wireOp",EDGE,"E22"),subQ1,sQuery(id+"F0.wireOp",EDGE,"E23.top"),sQuery(id+"F0.wireOp",EDGE,"E23.left"),subQ0])],"isStart":false})],"blendedInto":[makeQuery(id+"F1.opExtrude","CAP_FACE",FACE,{"disambiguationData":[OSD([sQuery(id+"F0.wireOp",EDGE,"E2"),sQuery(id+"F0.wireOp",EDGE,"E3"),sQuery(id+"F0.wireOp",EDGE,"E4"),sQuery(id+"F0.wireOp",EDGE,"E5"),sQuery(id+"F0.wireOp",EDGE,"E6"),sQuery(id+"F0.wireOp",EDGE,"E7"),sQuery(id+"F0.wireOp",EDGE,"E8"),sQuery(id+"F0.wireOp",EDGE,"E9"),sQuery(id+"F0.wireOp",EDGE,"E19"),sQuery(id+"F0.wireOp",EDGE,"E20"),sQuery(id+"F0.wireOp",EDGE,"E21"),sQuery(id+"F0.wireOp",EDGE,"E22"),subQ1,sQuery(id+"F0.wireOp",EDGE,"E23.top"),sQuery(id+"F0.wireOp",EDGE,"E23.left"),subQ0])],"isStart":false})]});}
            var Q14;
            {var subQ0=sQuery(id+"F0.wireOp",EDGE,"E23.right");var subQ1=sQuery(id+"F0.wireOp",EDGE,"E23.bottom");Q14=makeQuery(id+"F3.opFillet","BLEND_EDGE",EDGE,{"blendedFrom":[makeQuery(id+"F1.opExtrude","SWEPT_EDGE",EDGE,{"disambiguationData":[OSD([subQ1,subQ0])]}),makeQuery(id+"F1.opExtrude","CAP_FACE",FACE,{"disambiguationData":[OSD([sQuery(id+"F0.wireOp",EDGE,"E2"),sQuery(id+"F0.wireOp",EDGE,"E3"),sQuery(id+"F0.wireOp",EDGE,"E4"),sQuery(id+"F0.wireOp",EDGE,"E5"),sQuery(id+"F0.wireOp",EDGE,"E6"),sQuery(id+"F0.wireOp",EDGE,"E7"),sQuery(id+"F0.wireOp",EDGE,"E8"),sQuery(id+"F0.wireOp",EDGE,"E9"),sQuery(id+"F0.wireOp",EDGE,"E19"),sQuery(id+"F0.wireOp",EDGE,"E20"),sQuery(id+"F0.wireOp",EDGE,"E21"),sQuery(id+"F0.wireOp",EDGE,"E22"),subQ1,sQuery(id+"F0.wireOp",EDGE,"E23.top"),sQuery(id+"F0.wireOp",EDGE,"E23.left"),subQ0])],"isStart":true})],"blendedInto":[makeQuery(id+"F1.opExtrude","CAP_FACE",FACE,{"disambiguationData":[OSD([sQuery(id+"F0.wireOp",EDGE,"E2"),sQuery(id+"F0.wireOp",EDGE,"E3"),sQuery(id+"F0.wireOp",EDGE,"E4"),sQuery(id+"F0.wireOp",EDGE,"E5"),sQuery(id+"F0.wireOp",EDGE,"E6"),sQuery(id+"F0.wireOp",EDGE,"E7"),sQuery(id+"F0.wireOp",EDGE,"E8"),sQuery(id+"F0.wireOp",EDGE,"E9"),sQuery(id+"F0.wireOp",EDGE,"E19"),sQuery(id+"F0.wireOp",EDGE,"E20"),sQuery(id+"F0.wireOp",EDGE,"E21"),sQuery(id+"F0.wireOp",EDGE,"E22"),subQ1,sQuery(id+"F0.wireOp",EDGE,"E23.top"),sQuery(id+"F0.wireOp",EDGE,"E23.left"),subQ0])],"isStart":true})]});}
            var Q15;
            {var subQ0=sQuery(id+"F0.wireOp",EDGE,"E23.right");var subQ1=sQuery(id+"F0.wireOp",EDGE,"E23.top");Q15=makeQuery(id+"F3.opFillet","BLEND_EDGE",EDGE,{"blendedFrom":[makeQuery(id+"F1.opExtrude","SWEPT_EDGE",EDGE,{"disambiguationData":[OSD([subQ1,subQ0])]}),makeQuery(id+"F1.opExtrude","CAP_FACE",FACE,{"disambiguationData":[OSD([sQuery(id+"F0.wireOp",EDGE,"E2"),sQuery(id+"F0.wireOp",EDGE,"E3"),sQuery(id+"F0.wireOp",EDGE,"E4"),sQuery(id+"F0.wireOp",EDGE,"E5"),sQuery(id+"F0.wireOp",EDGE,"E6"),sQuery(id+"F0.wireOp",EDGE,"E7"),sQuery(id+"F0.wireOp",EDGE,"E8"),sQuery(id+"F0.wireOp",EDGE,"E9"),sQuery(id+"F0.wireOp",EDGE,"E19"),sQuery(id+"F0.wireOp",EDGE,"E20"),sQuery(id+"F0.wireOp",EDGE,"E21"),sQuery(id+"F0.wireOp",EDGE,"E22"),sQuery(id+"F0.wireOp",EDGE,"E23.bottom"),subQ1,sQuery(id+"F0.wireOp",EDGE,"E23.left"),subQ0])],"isStart":true})],"blendedInto":[makeQuery(id+"F1.opExtrude","CAP_FACE",FACE,{"disambiguationData":[OSD([sQuery(id+"F0.wireOp",EDGE,"E2"),sQuery(id+"F0.wireOp",EDGE,"E3"),sQuery(id+"F0.wireOp",EDGE,"E4"),sQuery(id+"F0.wireOp",EDGE,"E5"),sQuery(id+"F0.wireOp",EDGE,"E6"),sQuery(id+"F0.wireOp",EDGE,"E7"),sQuery(id+"F0.wireOp",EDGE,"E8"),sQuery(id+"F0.wireOp",EDGE,"E9"),sQuery(id+"F0.wireOp",EDGE,"E19"),sQuery(id+"F0.wireOp",EDGE,"E20"),sQuery(id+"F0.wireOp",EDGE,"E21"),sQuery(id+"F0.wireOp",EDGE,"E22"),sQuery(id+"F0.wireOp",EDGE,"E23.bottom"),subQ1,sQuery(id+"F0.wireOp",EDGE,"E23.left"),subQ0])],"isStart":true})]});}
            fillet(context, id + "F4", {"entities" : qUnion([Q0, Q1, Q2, Q3, Q4, Q5, Q6, Q7, Q8, Q9, Q10, Q11, Q12, Q13, Q14, Q15]), "radius" : 1 * mm, "tangentPropagation" : true, "allowEdgeOverflow" : false});
        }
    });
